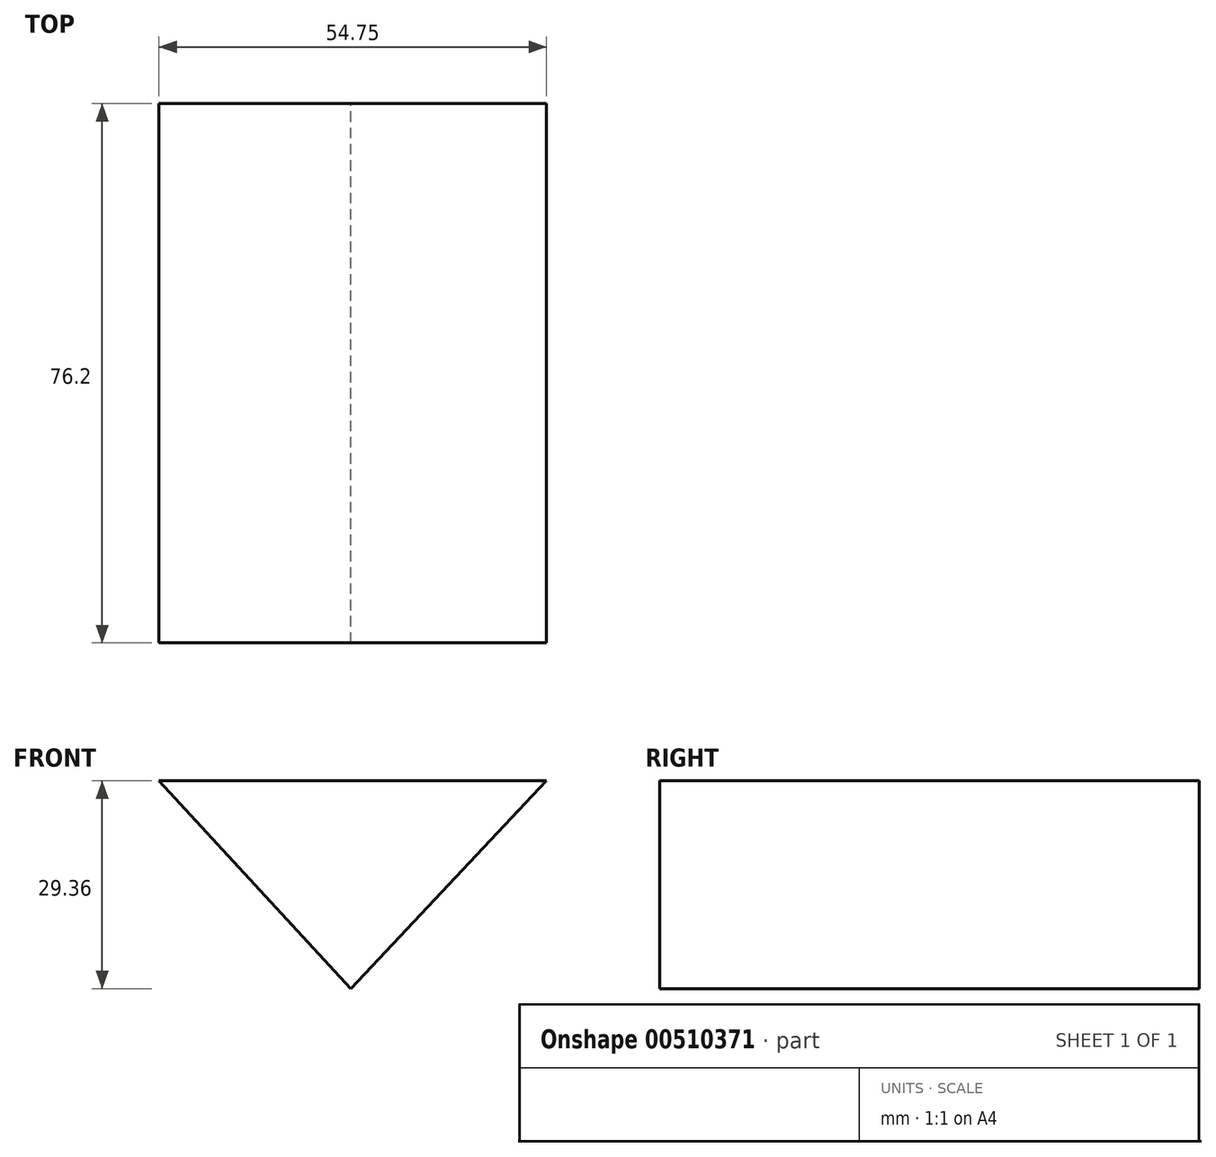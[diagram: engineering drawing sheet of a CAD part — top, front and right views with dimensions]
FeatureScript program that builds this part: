
annotation { "Feature Type Name" : "Feature", "Feature Type Description" : "" }
export const myFeature = defineFeature(function(context is Context, id is Id, definition is map)
    precondition{}
    {
        {
            var Q0;
            Q0=qCreatedBy(makeId("Front.planeOp"),FACE);
            var sketch = newSketch(context, id + "F0", { "sketchPlane" : qUnion([Q0])});
            skLineSegment(sketch, "E0", {"start": v(-27.11, 29.36) * mm, "end": v(27.64, 29.36) * mm});
            skLineSegment(sketch, "E1", {"start": v(-27.11, 29.36) * mm, "end": v(0, 0) * mm});
            skLineSegment(sketch, "E2", {"start": v(0, 0) * mm, "end": v(27.64, 29.36) * mm});
            skSolve(sketch);
        }
        {
            var Q0;
            Q0=makeQuery(id+"F0.imprint","IMPRINT",FACE,{"disambiguationData":[TD([[makeQuery(id+"F0.imprint","IMPRINT",EDGE,{"derivedFrom":sQuery(id+"F0.wireOp",EDGE,"E0")}),-1.0]])]});
            extrude(context, id + "F1", {"entities" : qUnion([Q0]), "depth" : 76.2 * mm});
        }
    });
